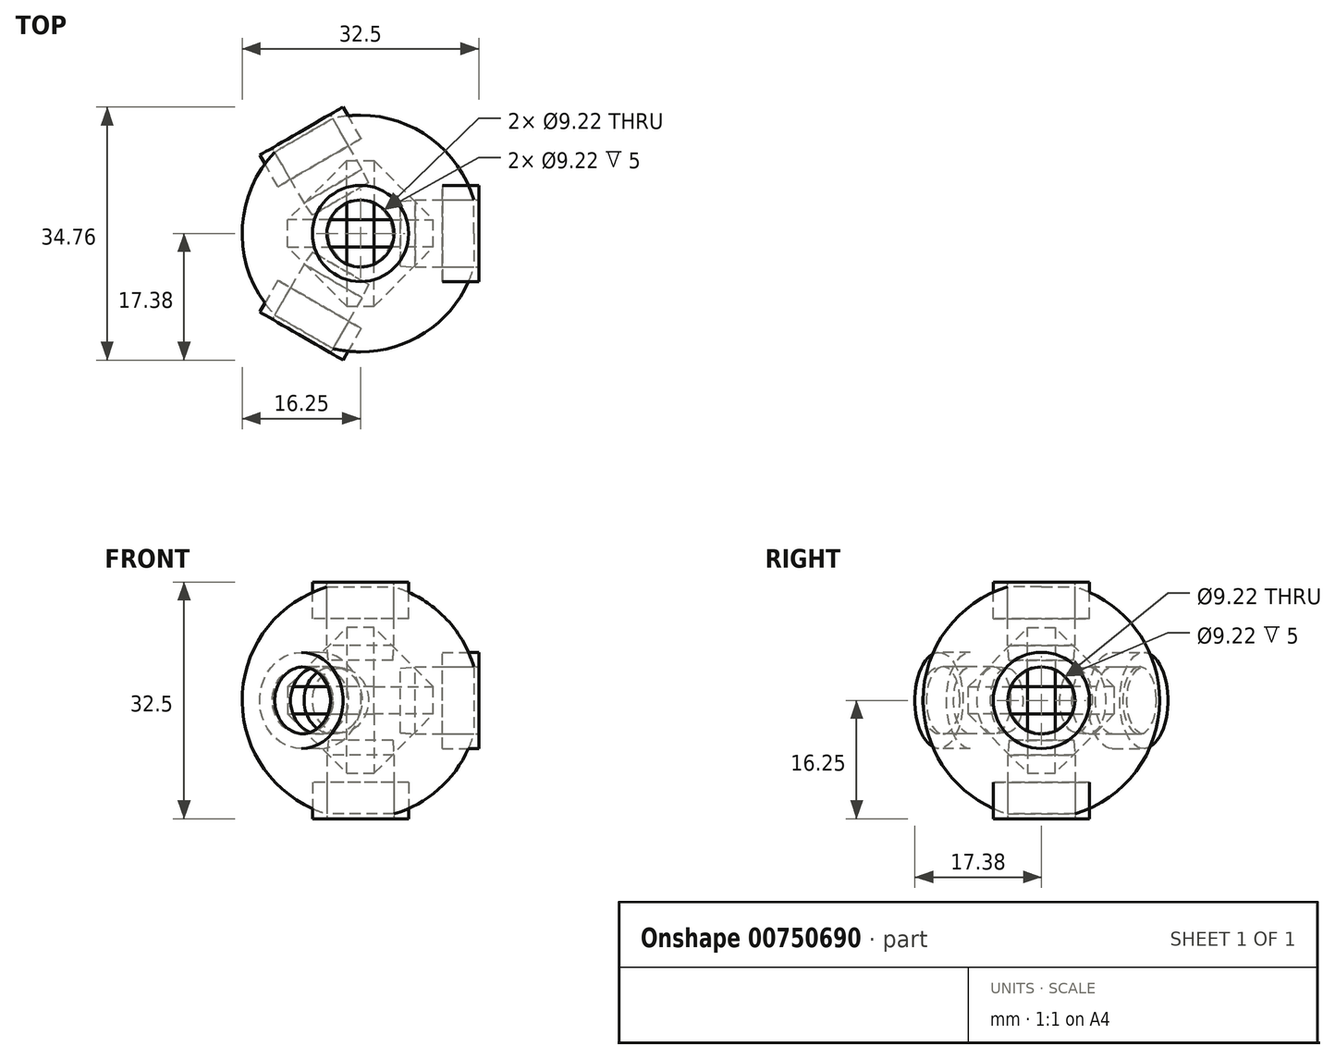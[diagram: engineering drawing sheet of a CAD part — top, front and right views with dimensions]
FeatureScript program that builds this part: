
annotation { "Feature Type Name" : "Feature", "Feature Type Description" : "" }
export const myFeature = defineFeature(function(context is Context, id is Id, definition is map)
    precondition{}
    {
        {
            assignVariable(context, id + "F0", {"name" : "Height", "anyValue" : 32.5});
        }
        {
            var Q0;
            Q0=qCreatedBy(makeId("Front.planeOp"),FACE);
            var sketch = newSketch(context, id + "F1", { "sketchPlane" : qUnion([Q0])});
            skLineSegment(sketch, "E0.bottom", {"start": v(-10, -10) * mm, "end": v(10, -10) * mm});
            skLineSegment(sketch, "E0.top", {"start": v(-10, 10) * mm, "end": v(10, 10) * mm});
            skLineSegment(sketch, "E0.left", {"start": v(-10, -10) * mm, "end": v(-10, 10) * mm});
            skLineSegment(sketch, "E0.right", {"start": v(10, -10) * mm, "end": v(10, 10) * mm});
            skPoint(sketch, "E0.middle", {"position": v(0, 0) * mm});
            skSolve(sketch);
        }
        {
            var Q0;
            Q0=makeQuery(id+"F1.imprint","IMPRINT",FACE,{"disambiguationData":[TD([[makeQuery(id+"F1.imprint","IMPRINT",EDGE,{"derivedFrom":sQuery(id+"F1.wireOp",EDGE,"E0.bottom")}),1.0]])]});
            extrude(context, id + "F2", {"entities" : qUnion([Q0]), "endBound" : BoundingType.SYMMETRIC, "depth" : 20 * mm, "offsetDistance" : 25 * mm});
        }
        {
            var Q0;
            Q0=makeQuery(id+"F2.opExtrude","SWEPT_FACE",FACE,{"disambiguationData":[OSD([sQuery(id+"F1.wireOp",EDGE,"E0.left")])]});
            var Q1;
            Q1=makeQuery(id+"F2.opExtrude","SWEPT_FACE",FACE,{"disambiguationData":[OSD([sQuery(id+"F1.wireOp",EDGE,"E0.right")])]});
            var Q2;
            Q2=makeQuery(id+"F2.opExtrude","SWEPT_FACE",FACE,{"disambiguationData":[OSD([sQuery(id+"F1.wireOp",EDGE,"E0.top")])]});
            var Q3;
            Q3=makeQuery(id+"F2.opExtrude","SWEPT_FACE",FACE,{"disambiguationData":[OSD([sQuery(id+"F1.wireOp",EDGE,"E0.bottom")])]});
            chamfer(context, id + "F3", {"entities" : qUnion([Q0, Q1, Q2, Q3]), "width" : getVariable(context, 'Height') / 4 * mm, "tangentPropagation" : true});
        }
        {
            var Q0;
            Q0=qCreatedBy(makeId("Top.planeOp"),FACE);
            var sketch = newSketch(context, id + "F4", { "sketchPlane" : qUnion([Q0])});
            skCircle(sketch, "E1", {"center": v(0, 0) * mm, "radius": 16.25 * mm});
            skLineSegment(sketch, "E2", {"start": v(0, -16.25) * mm, "end": v(0, 16.25) * mm});
            skSolve(sketch);
        }
        {
            var Q0;
            {var subQ0=sQuery(id+"F4.wireOp",EDGE,"E2");Q0=makeQuery(id+"F4.imprint","IMPRINT",FACE,{"disambiguationData":[TD([[makeQuery(id+"F4.imprint","IMPRINT",EDGE,{"derivedFrom":subQ0}),-1.0]])]});}
            var Q1;
            Q1=sQuery(id+"F4.wireOp",EDGE,"E2");
            revolve(context, id + "F5", {"surfaceOperationType" : NewSurfaceOperationType.NEW, "entities" : qUnion([Q0]), "axis" : qUnion([Q1]), "revolveType" : RevolveType.FULL});
        }
        {
            var Q0;
            Q0=qCreatedBy(makeId("Top.planeOp"),FACE);
            cPlane(context, id + "F6", {"entities" : qUnion([Q0]), "cplaneType" : CPlaneType.OFFSET, "offset" : getVariable(context, 'Height') / 2 * mm, "width" : 150 * mm, "height" : 150 * mm});
        }
        {
            var Q0;
            Q0=qCreatedBy(id+"F6.planeOp",FACE);
            var sketch = newSketch(context, id + "F7", { "sketchPlane" : qUnion([Q0])});
            skCircle(sketch, "E3", {"center": v(0, 0) * mm, "radius": 4.61 * mm});
            skCircle(sketch, "E4", {"center": v(0, 0) * mm, "radius": 6.61 * mm});
            skSolve(sketch);
        }
        {
            var Q0;
            Q0=makeQuery(id+"F7.imprint","IMPRINT",FACE,{"disambiguationData":[TD([[makeQuery(id+"F7.imprint","IMPRINT",EDGE,{"derivedFrom":sQuery(id+"F7.wireOp",EDGE,"E3")}),1.0]])]});
            extrude(context, id + "F8", {"entities" : qUnion([Q0]), "oppositeDirection" : true, "depth" : 10.75 * mm, "offsetDistance" : 25 * mm});
        }
        {
            var Q0;
            Q0=makeQuery(id+"F8.opExtrude","CAP_FACE",FACE,{"disambiguationData":[OSD([sQuery(id+"F7.wireOp",EDGE,"E3")])],"isStart":false});
            chamfer(context, id + "F9", {"entities" : qUnion([Q0]), "chamferType" : ChamferType.OFFSET_ANGLE, "width" : 0.18 * mm, "oppositeDirection" : true, "angle" : 85 * degree, "tangentPropagation" : true});
        }
        {
            var Q0;
            Q0=makeQuery(id+"F7.imprint","IMPRINT",FACE,{"disambiguationData":[TD([[makeQuery(id+"F7.imprint","IMPRINT",EDGE,{"derivedFrom":sQuery(id+"F7.wireOp",EDGE,"E3")}),-1.0]])]});
            extrude(context, id + "F10", {"entities" : qUnion([Q0]), "oppositeDirection" : true, "depth" : 5 * mm, "offsetDistance" : 25 * mm});
        }
        {
            var Q0;
            Q0=makeQuery(id+"F10.opExtrude","SWEPT_BODY",BODY,{"disambiguationData":[OSD([sQuery(id+"F7.wireOp",EDGE,"E3"),sQuery(id+"F7.wireOp",EDGE,"E4")])]});
            var Q1;
            Q1=makeQuery(id+"F8.opExtrude","SWEPT_BODY",BODY,{"disambiguationData":[OSD([sQuery(id+"F7.wireOp",EDGE,"E3")])]});
            var Q2;
            Q2=qCreatedBy(makeId("Top.planeOp"),FACE);
            mirror(context, id + "F11", {"entities" : qUnion([Q0, Q1]), "mirrorPlane" : qUnion([Q2])});
        }
        {
            var Q0;
            Q0=qCreatedBy(makeId("Top.planeOp"),FACE);
            var sketch = newSketch(context, id + "F12", { "sketchPlane" : qUnion([Q0])});
            skLineSegment(sketch, "E5", {"start": v(0, 0) * mm, "end": v(26.37, 0) * mm, "construction": true});
            skLineSegment(sketch, "E6", {"start": v(0, 0) * mm, "end": v(0, 38.93) * mm, "construction": true});
            skSolve(sketch);
        }
        {
            var Q0;
            Q0=qCreatedBy(makeId("Right.planeOp"),FACE);
            var sketch = newSketch(context, id + "F13", { "sketchPlane" : qUnion([Q0])});
            skLineSegment(sketch, "E7", {"start": v(0, 0) * mm, "end": v(0, 47.25) * mm, "construction": true});
            skSolve(sketch);
        }
        {
            var Q0;
            Q0=makeQuery(id+"F11.opPattern","COPY",BODY,{"derivedFrom":makeQuery(id+"F10.opExtrude","SWEPT_BODY",BODY,{"disambiguationData":[OSD([sQuery(id+"F7.wireOp",EDGE,"E3"),sQuery(id+"F7.wireOp",EDGE,"E4")])]}),"instanceName":"1"});
            var Q1;
            Q1=makeQuery(id+"F11.opPattern","COPY",BODY,{"derivedFrom":makeQuery(id+"F8.opExtrude","SWEPT_BODY",BODY,{"disambiguationData":[OSD([sQuery(id+"F7.wireOp",EDGE,"E3")])]}),"instanceName":"1"});
            var Q2;
            Q2=makeQuery(id+"F8.opExtrude","SWEPT_BODY",BODY,{"disambiguationData":[OSD([sQuery(id+"F7.wireOp",EDGE,"E3")])]});
            var Q3;
            Q3=makeQuery(id+"F10.opExtrude","SWEPT_BODY",BODY,{"disambiguationData":[OSD([sQuery(id+"F7.wireOp",EDGE,"E3"),sQuery(id+"F7.wireOp",EDGE,"E4")])]});
            var Q4;
            Q4=sQuery(id+"F12.wireOp",EDGE,"E6");
            transform(context, id + "F14", {"entities" : qUnion([Q0, Q1, Q2, Q3]), "transformType" : TransformType.ROTATION, "transformAxis" : qUnion([Q4]), "angle" : 90 * degree, "makeCopy" : true});
        }
        {
            var Q0;
            Q0=makeQuery(id+"F14.opPattern","COPY",BODY,{"derivedFrom":makeQuery(id+"F11.opPattern","COPY",BODY,{"derivedFrom":makeQuery(id+"F8.opExtrude","SWEPT_BODY",BODY,{"disambiguationData":[OSD([sQuery(id+"F7.wireOp",EDGE,"E3")])]}),"instanceName":"1"}),"instanceName":"1"});
            var Q1;
            Q1=makeQuery(id+"F14.opPattern","COPY",BODY,{"derivedFrom":makeQuery(id+"F11.opPattern","COPY",BODY,{"derivedFrom":makeQuery(id+"F10.opExtrude","SWEPT_BODY",BODY,{"disambiguationData":[OSD([sQuery(id+"F7.wireOp",EDGE,"E3"),sQuery(id+"F7.wireOp",EDGE,"E4")])]}),"instanceName":"1"}),"instanceName":"1"});
            deleteBodies(context, id + "F15", {"entities" : qUnion([Q0, Q1])});
        }
        {
            var Q0;
            Q0=makeQuery(id+"F14.opPattern","COPY",BODY,{"derivedFrom":makeQuery(id+"F8.opExtrude","SWEPT_BODY",BODY,{"disambiguationData":[OSD([sQuery(id+"F7.wireOp",EDGE,"E3")])]}),"instanceName":"1"});
            var Q1;
            Q1=makeQuery(id+"F14.opPattern","COPY",BODY,{"derivedFrom":makeQuery(id+"F10.opExtrude","SWEPT_BODY",BODY,{"disambiguationData":[OSD([sQuery(id+"F7.wireOp",EDGE,"E3"),sQuery(id+"F7.wireOp",EDGE,"E4")])]}),"instanceName":"1"});
            var Q2;
            Q2=sQuery(id+"F13.wireOp",EDGE,"E7");
            circularPattern(context, id + "F16", {"entities" : qUnion([Q0, Q1]), "axis" : qUnion([Q2]), "angle" : 360 * degree, "instanceCount" : 3, "equalSpace" : true});
        }
        {
            var Q0;
            Q0=makeQuery(id+"F8.opExtrude","SWEPT_BODY",BODY,{"disambiguationData":[OSD([sQuery(id+"F7.wireOp",EDGE,"E3")])]});
            var Q1;
            Q1=makeQuery(id+"F14.opPattern","COPY",BODY,{"derivedFrom":makeQuery(id+"F8.opExtrude","SWEPT_BODY",BODY,{"disambiguationData":[OSD([sQuery(id+"F7.wireOp",EDGE,"E3")])]}),"instanceName":"1"});
            var Q2;
            Q2=makeQuery(id+"F16.opPattern","COPY",BODY,{"derivedFrom":makeQuery(id+"F14.opPattern","COPY",BODY,{"derivedFrom":makeQuery(id+"F8.opExtrude","SWEPT_BODY",BODY,{"disambiguationData":[OSD([sQuery(id+"F7.wireOp",EDGE,"E3")])]}),"instanceName":"1"}),"instanceName":"1"});
            var Q3;
            Q3=makeQuery(id+"F11.opPattern","COPY",BODY,{"derivedFrom":makeQuery(id+"F8.opExtrude","SWEPT_BODY",BODY,{"disambiguationData":[OSD([sQuery(id+"F7.wireOp",EDGE,"E3")])]}),"instanceName":"1"});
            var Q4;
            Q4=makeQuery(id+"F16.opPattern","COPY",BODY,{"derivedFrom":makeQuery(id+"F14.opPattern","COPY",BODY,{"derivedFrom":makeQuery(id+"F8.opExtrude","SWEPT_BODY",BODY,{"disambiguationData":[OSD([sQuery(id+"F7.wireOp",EDGE,"E3")])]}),"instanceName":"1"}),"instanceName":"2"});
            var Q5;
            Q5=makeQuery(id+"F5.opRevolve","SWEPT_BODY",BODY,{"disambiguationData":[OSD([sQuery(id+"F4.wireOp",EDGE,"E1"),sQuery(id+"F4.wireOp",EDGE,"E2")])]});
            booleanBodies(context, id + "F17", {"operationType" : BooleanOperationType.SUBTRACTION, "tools" : qUnion([Q0, Q1, Q2, Q3, Q4]), "targets" : qUnion([Q5])});
        }
    });
